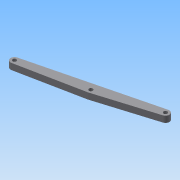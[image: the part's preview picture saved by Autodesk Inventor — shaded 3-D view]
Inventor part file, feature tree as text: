
AUTODESK INVENTOR PART (.ipt)
format: ipt  version: 2015 (Build 190159000, 159)  size: 95,744 bytes
history: native  units: mm
features: extrude x2, sketch x2, other x1
ambient origin geometry x8: Origin, YZ Plane, XZ Plane, XY Plane, X Axis, Y Axis, Z Axis, Center Point
bodies: Body1 (feature_tree)
feature tree (5):
  other  "實體1"
  extrude  "擠出1"  Depth=20.85mm
  extrude  "擠出2"  Depth=40.0mm
  sketch  "草圖1"
  sketch  "草圖2"
